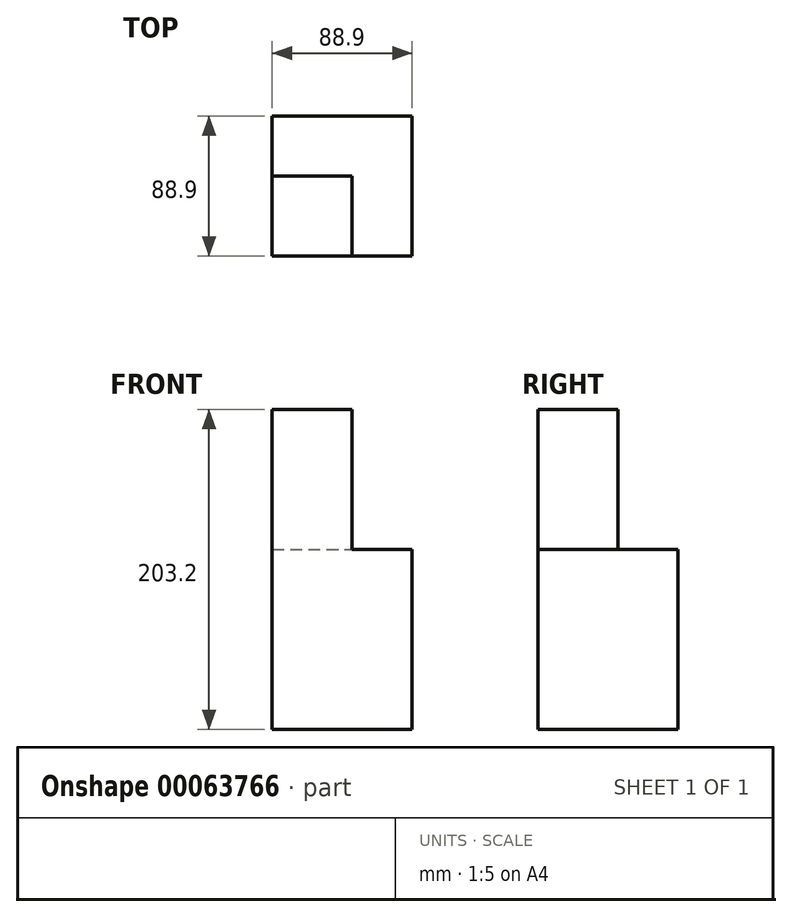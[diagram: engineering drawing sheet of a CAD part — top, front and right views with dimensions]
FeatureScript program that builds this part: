
annotation { "Feature Type Name" : "Feature", "Feature Type Description" : "" }
export const myFeature = defineFeature(function(context is Context, id is Id, definition is map)
    precondition{}
    {
        {
            var Q0;
            Q0=qCreatedBy(makeId("Top.planeOp"),FACE);
            var sketch = newSketch(context, id + "F0", { "sketchPlane" : qUnion([Q0])});
            skLineSegment(sketch, "E0.bottom", {"start": v(-41.76, 43.96) * mm, "end": v(47.14, 43.96) * mm});
            skLineSegment(sketch, "E0.top", {"start": v(-41.76, -44.94) * mm, "end": v(47.14, -44.94) * mm});
            skLineSegment(sketch, "E0.left", {"start": v(-41.76, 43.96) * mm, "end": v(-41.76, -44.94) * mm});
            skLineSegment(sketch, "E0.right", {"start": v(47.14, 43.96) * mm, "end": v(47.14, -44.94) * mm});
            skSolve(sketch);
        }
        {
            var Q0;
            Q0 = qSketchRegion(id + "F0", true);
            extrude(context, id + "F1", {"entities" : qUnion([Q0]), "depth" : 203.2 * mm});
        }
        {
            var Q0;
            Q0=makeQuery(id+"F1.opExtrude","CAP_FACE",FACE,{"disambiguationData":[OSD([sQuery(id+"F0.wireOp",EDGE,"E0.bottom"),sQuery(id+"F0.wireOp",EDGE,"E0.top"),sQuery(id+"F0.wireOp",EDGE,"E0.left"),sQuery(id+"F0.wireOp",EDGE,"E0.right")])],"isStart":false});
            var sketch = newSketch(context, id + "F2", { "sketchPlane" : qUnion([Q0])});
            skLineSegment(sketch, "E1.0", {"start": v(-41.76, 43.96) * mm, "end": v(47.14, 43.96) * mm});
            skLineSegment(sketch, "E2.0", {"start": v(47.14, 43.96) * mm, "end": v(47.14, -44.94) * mm});
            skLineSegment(sketch, "E3.top", {"start": v(-41.76, 5.86) * mm, "end": v(9.04, 5.86) * mm});
            skLineSegment(sketch, "E3.left", {"start": v(-41.76, 43.96) * mm, "end": v(-41.76, 5.86) * mm});
            skLineSegment(sketch, "E3.right", {"start": v(47.14, 43.96) * mm, "end": v(47.14, 5.86) * mm});
            skLineSegment(sketch, "E4.bottom", {"start": v(47.14, 43.96) * mm, "end": v(9.04, 43.96) * mm});
            skLineSegment(sketch, "E4.top", {"start": v(47.14, -44.94) * mm, "end": v(9.04, -44.94) * mm});
            skLineSegment(sketch, "E4.right", {"start": v(9.04, 5.86) * mm, "end": v(9.04, -44.94) * mm});
            skSolve(sketch);
        }
        {
            var Q0;
            Q0 = qSketchRegion(id + "F2", true);
            extrude(context, id + "F3", {"entities" : qUnion([Q0]), "operationType" : NewBodyOperationType.REMOVE, "oppositeDirection" : true, "depth" : 88.9 * mm});
        }
    });
